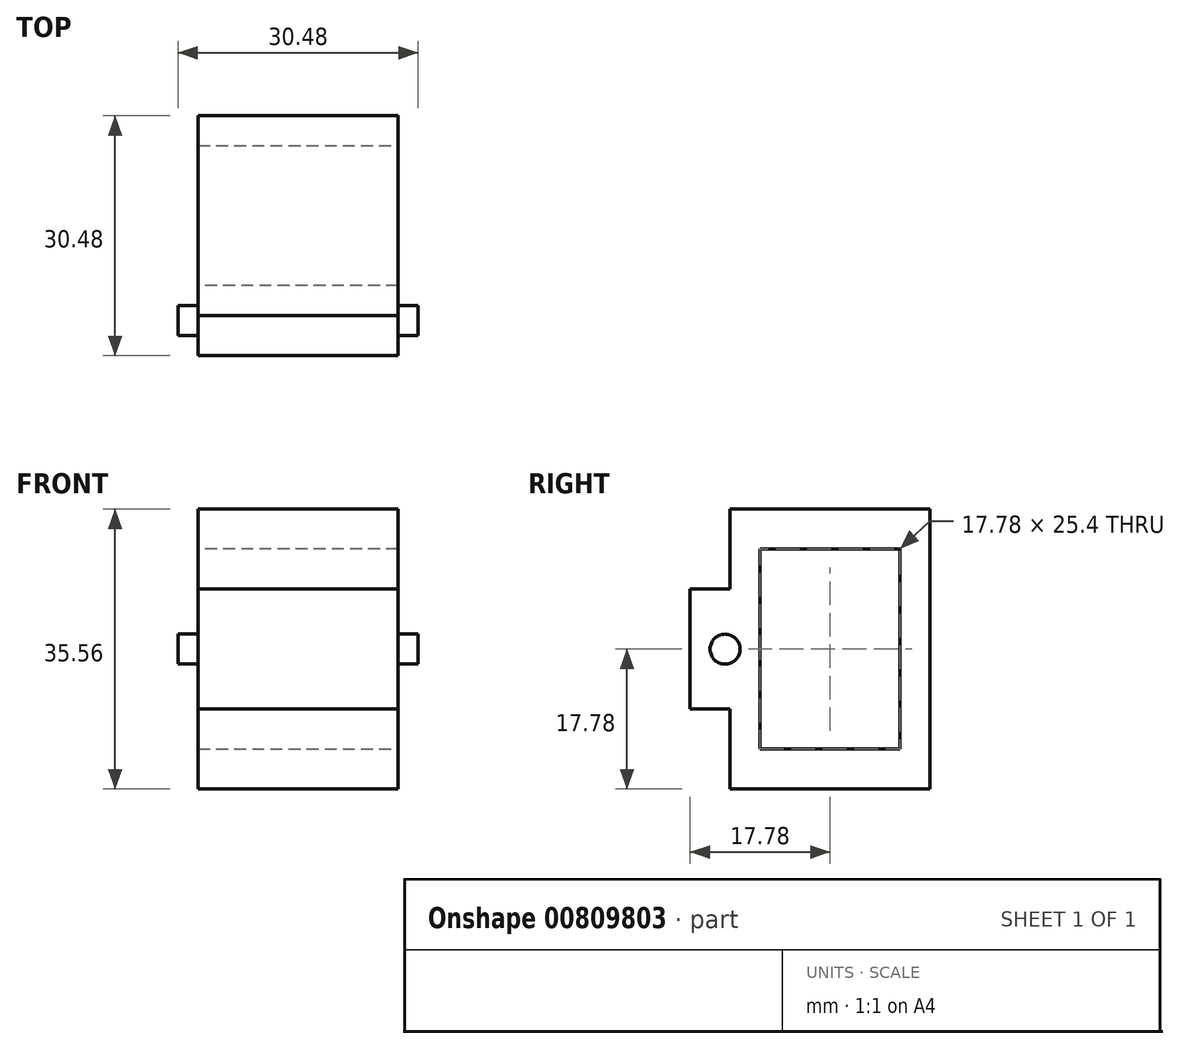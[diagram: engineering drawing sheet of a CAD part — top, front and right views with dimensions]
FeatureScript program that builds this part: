
annotation { "Feature Type Name" : "Feature", "Feature Type Description" : "" }
export const myFeature = defineFeature(function(context is Context, id is Id, definition is map)
    precondition{}
    {
        {
            var Q0;
            Q0=qCreatedBy(makeId("Top.planeOp"),FACE);
            var sketch = newSketch(context, id + "F0", { "sketchPlane" : qUnion([Q0])});
            skLineSegment(sketch, "E0", {"start": v(0, 0) * mm, "end": v(0, -17.78) * mm});
            skLineSegment(sketch, "E1", {"start": v(0, 0) * mm, "end": v(0, 7.62) * mm});
            skLineSegment(sketch, "E2", {"start": v(0, 0) * mm, "end": v(-25.4, 0) * mm});
            skLineSegment(sketch, "E3", {"start": v(-25.4, 0) * mm, "end": v(-25.4, -17.78) * mm});
            skLineSegment(sketch, "E4", {"start": v(-25.4, 0) * mm, "end": v(-25.4, 7.62) * mm});
            skLineSegment(sketch, "E5", {"start": v(-25.4, -17.78) * mm, "end": v(0, -17.78) * mm});
            skLineSegment(sketch, "E6", {"start": v(-25.4, 7.62) * mm, "end": v(0, 7.62) * mm});
            skSolve(sketch);
        }
        {
            var Q0;
            Q0=qSketchRegion(id+"F0",true);
            extrude(context, id + "F1", {"entities" : qUnion([Q0]), "depth" : 5.08 * mm, "offsetDistance" : 25.4 * mm});
        }
        {
            var Q0;
            Q0=makeQuery(id+"F1.opExtrude","CAP_FACE",FACE,{"disambiguationData":[OSD([sQuery(id+"F0.wireOp",EDGE,"E0"),sQuery(id+"F0.wireOp",EDGE,"E1"),sQuery(id+"F0.wireOp",EDGE,"E3"),sQuery(id+"F0.wireOp",EDGE,"E4"),sQuery(id+"F0.wireOp",EDGE,"E5"),sQuery(id+"F0.wireOp",EDGE,"E6")])],"isStart":false});
            var sketch = newSketch(context, id + "F2", { "sketchPlane" : qUnion([Q0])});
            skLineSegment(sketch, "E7", {"start": v(0, -17.78) * mm, "end": v(0, -13.97) * mm});
            skLineSegment(sketch, "E8", {"start": v(0, -13.97) * mm, "end": v(-25.4, -13.97) * mm});
            skLineSegment(sketch, "E9", {"start": v(-25.4, -13.97) * mm, "end": v(-25.4, -17.78) * mm});
            skLineSegment(sketch, "E10", {"start": v(-25.4, -17.78) * mm, "end": v(0, -17.78) * mm});
            skLineSegment(sketch, "E11", {"start": v(-25.4, 7.62) * mm, "end": v(-25.4, 3.8) * mm});
            skLineSegment(sketch, "E12", {"start": v(-25.4, 3.8) * mm, "end": v(0, 3.8) * mm});
            skLineSegment(sketch, "E13", {"start": v(0, 3.8) * mm, "end": v(0, 7.62) * mm});
            skLineSegment(sketch, "E14", {"start": v(0, 7.62) * mm, "end": v(-25.4, 7.62) * mm});
            skSolve(sketch);
        }
        {
            var Q0;
            Q0=qSketchRegion(id+"F2",true);
            extrude(context, id + "F3", {"entities" : qUnion([Q0]), "operationType" : NewBodyOperationType.ADD, "depth" : 25.4 * mm, "offsetDistance" : 25.4 * mm});
        }
        {
            var Q0;
            Q0=makeQuery(id+"F3.opExtrude","CAP_FACE",FACE,{"disambiguationData":[OSD([sQuery(id+"F2.wireOp",EDGE,"E7"),sQuery(id+"F2.wireOp",EDGE,"E8"),sQuery(id+"F2.wireOp",EDGE,"E9"),sQuery(id+"F2.wireOp",EDGE,"E10")])],"isStart":false});
            var sketch = newSketch(context, id + "F4", { "sketchPlane" : qUnion([Q0])});
            skLineSegment(sketch, "E15", {"start": v(0, -17.78) * mm, "end": v(0, 7.62) * mm});
            skLineSegment(sketch, "E16", {"start": v(0, -17.78) * mm, "end": v(-25.4, -17.78) * mm});
            skLineSegment(sketch, "E17", {"start": v(-25.4, -17.78) * mm, "end": v(-25.4, 7.62) * mm});
            skLineSegment(sketch, "E18", {"start": v(-25.4, 7.62) * mm, "end": v(0, 7.62) * mm});
            skSolve(sketch);
        }
        {
            var Q0;
            Q0=qSketchRegion(id+"F4",true);
            extrude(context, id + "F5", {"entities" : qUnion([Q0]), "operationType" : NewBodyOperationType.ADD, "depth" : 5.08 * mm, "offsetDistance" : 25.4 * mm});
        }
        {
            var Q0;
            Q0=makeQuery(id+"F5.boolean.opBoolean","MERGE",FACE,{"derivedFrom":[makeQuery(id+"F3.boolean.opBoolean","MERGE",FACE,{"derivedFrom":[makeQuery(id+"F1.opExtrude","SWEPT_FACE",FACE,{"disambiguationData":[OSD([sQuery(id+"F0.wireOp",EDGE,"E5")])]}),makeQuery(id+"F3.opExtrude","SWEPT_FACE",FACE,{"disambiguationData":[OSD([sQuery(id+"F2.wireOp",EDGE,"E10")])]})]}),makeQuery(id+"F5.opExtrude","SWEPT_FACE",FACE,{"disambiguationData":[OSD([sQuery(id+"F4.wireOp",EDGE,"E16")])]})]});
            var sketch = newSketch(context, id + "F6", { "sketchPlane" : qUnion([Q0])});
            skLineSegment(sketch, "E19", {"start": v(-25.4, 35.56) * mm, "end": v(-25.4, 25.4) * mm});
            skLineSegment(sketch, "E20", {"start": v(-25.4, 0) * mm, "end": v(-25.4, 10.16) * mm});
            skLineSegment(sketch, "E21", {"start": v(0, 35.56) * mm, "end": v(0, 25.4) * mm});
            skLineSegment(sketch, "E22", {"start": v(0, 0) * mm, "end": v(0, 10.16) * mm});
            skLineSegment(sketch, "E23", {"start": v(-25.4, 25.4) * mm, "end": v(0, 25.4) * mm});
            skLineSegment(sketch, "E24", {"start": v(0, 10.16) * mm, "end": v(-25.4, 10.16) * mm});
            skLineSegment(sketch, "E25", {"start": v(-25.4, 25.4) * mm, "end": v(-25.4, 10.16) * mm});
            skLineSegment(sketch, "E26", {"start": v(0, 10.16) * mm, "end": v(0, 25.4) * mm});
            skSolve(sketch);
        }
        {
            var Q0;
            Q0=qSketchRegion(id+"F6",true);
            extrude(context, id + "F7", {"entities" : qUnion([Q0]), "operationType" : NewBodyOperationType.ADD, "depth" : 5.08 * mm, "offsetDistance" : 25.4 * mm});
        }
        {
            var Q0;
            Q0=makeQuery(id+"F7.boolean.opBoolean","MERGE",FACE,{"derivedFrom":[makeQuery(id+"F5.boolean.opBoolean","MERGE",FACE,{"derivedFrom":[makeQuery(id+"F3.boolean.opBoolean","MERGE",FACE,{"derivedFrom":[makeQuery(id+"F1.opExtrude","SWEPT_FACE",FACE,{"disambiguationData":[OSD([sQuery(id+"F0.wireOp",EDGE,"E0"),sQuery(id+"F0.wireOp",EDGE,"E1")])]}),makeQuery(id+"F3.opExtrude","SWEPT_FACE",FACE,{"disambiguationData":[OSD([sQuery(id+"F2.wireOp",EDGE,"E7")])]}),makeQuery(id+"F3.opExtrude","SWEPT_FACE",FACE,{"disambiguationData":[OSD([sQuery(id+"F2.wireOp",EDGE,"E13")])]})]}),makeQuery(id+"F5.opExtrude","SWEPT_FACE",FACE,{"disambiguationData":[OSD([sQuery(id+"F4.wireOp",EDGE,"E15")])]})]}),makeQuery(id+"F7.opExtrude","SWEPT_FACE",FACE,{"disambiguationData":[OSD([sQuery(id+"F6.wireOp",EDGE,"E26")])]})]});
            var sketch = newSketch(context, id + "F8", { "sketchPlane" : qUnion([Q0])});
            skLineSegment(sketch, "E27", {"start": v(-22.86, 17.78) * mm, "end": v(-13.97, 17.78) * mm});
            skLineSegment(sketch, "E28", {"start": v(-13.97, 17.78) * mm, "end": v(-18.41, 17.78) * mm});
            skCircle(sketch, "E29", {"center": v(-18.41, 17.78) * mm, "radius": 1.9 * mm});
            skSolve(sketch);
        }
        {
            var Q0;
            Q0=qSketchRegion(id+"F8",true);
            extrude(context, id + "F9", {"entities" : qUnion([Q0]), "operationType" : NewBodyOperationType.ADD, "depth" : 2.54 * mm, "offsetDistance" : 25.4 * mm});
        }
        {
            var Q0;
            Q0=makeQuery(id+"F7.boolean.opBoolean","MERGE",FACE,{"derivedFrom":[makeQuery(id+"F5.boolean.opBoolean","MERGE",FACE,{"derivedFrom":[makeQuery(id+"F3.boolean.opBoolean","MERGE",FACE,{"derivedFrom":[makeQuery(id+"F1.opExtrude","SWEPT_FACE",FACE,{"disambiguationData":[OSD([sQuery(id+"F0.wireOp",EDGE,"E3"),sQuery(id+"F0.wireOp",EDGE,"E4")])]}),makeQuery(id+"F3.opExtrude","SWEPT_FACE",FACE,{"disambiguationData":[OSD([sQuery(id+"F2.wireOp",EDGE,"E9")])]}),makeQuery(id+"F3.opExtrude","SWEPT_FACE",FACE,{"disambiguationData":[OSD([sQuery(id+"F2.wireOp",EDGE,"E11")])]})]}),makeQuery(id+"F5.opExtrude","SWEPT_FACE",FACE,{"disambiguationData":[OSD([sQuery(id+"F4.wireOp",EDGE,"E17")])]})]}),makeQuery(id+"F7.opExtrude","SWEPT_FACE",FACE,{"disambiguationData":[OSD([sQuery(id+"F6.wireOp",EDGE,"E25")])]})]});
            var sketch = newSketch(context, id + "F10", { "sketchPlane" : qUnion([Q0])});
            skLineSegment(sketch, "E30", {"start": v(22.86, 17.78) * mm, "end": v(13.97, 17.78) * mm});
            skLineSegment(sketch, "E31", {"start": v(13.97, 17.78) * mm, "end": v(18.41, 17.78) * mm});
            skCircle(sketch, "E32", {"center": v(18.41, 17.78) * mm, "radius": 1.9 * mm});
            skSolve(sketch);
        }
        {
            var Q0;
            Q0=qSketchRegion(id+"F10",true);
            extrude(context, id + "F11", {"entities" : qUnion([Q0]), "operationType" : NewBodyOperationType.ADD, "depth" : 2.54 * mm, "offsetDistance" : 25.4 * mm});
        }
    });
